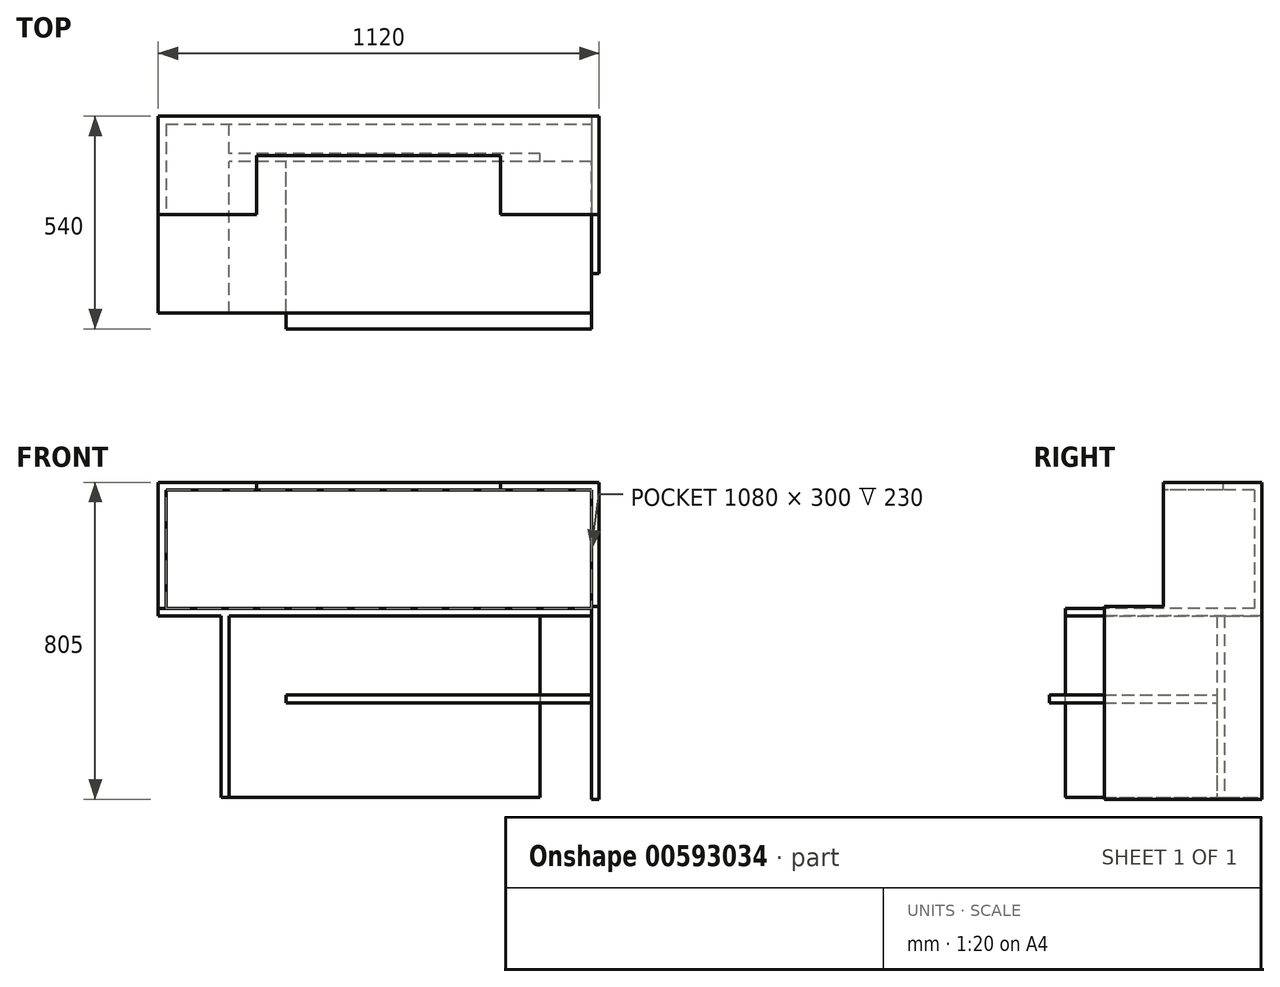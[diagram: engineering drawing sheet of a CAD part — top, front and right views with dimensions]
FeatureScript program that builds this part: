
annotation { "Feature Type Name" : "Feature", "Feature Type Description" : "" }
export const myFeature = defineFeature(function(context is Context, id is Id, definition is map)
    precondition{}
    {
        {
            var Q0;
            Q0=qCreatedBy(makeId("Top.planeOp"),FACE);
            var sketch = newSketch(context, id + "F0", { "sketchPlane" : qUnion([Q0])});
            skLineSegment(sketch, "E0.bottom", {"start": v(550, 250) * mm, "end": v(-550, 250) * mm});
            skLineSegment(sketch, "E0.top", {"start": v(550, -250) * mm, "end": v(-550, -250) * mm});
            skLineSegment(sketch, "E0.left", {"start": v(550, 250) * mm, "end": v(550, -250) * mm});
            skLineSegment(sketch, "E0.right", {"start": v(-550, 250) * mm, "end": v(-550, -250) * mm});
            skPoint(sketch, "E0.middle", {"position": v(0, 0) * mm});
            skSolve(sketch);
        }
        {
            var Q0;
            Q0=makeQuery(id+"F0.imprint","IMPRINT",FACE,{"disambiguationData":[TD([[makeQuery(id+"F0.imprint","IMPRINT",EDGE,{"derivedFrom":sQuery(id+"F0.wireOp",EDGE,"E0.bottom")}),1.0]])]});
            extrude(context, id + "F1", {"entities" : qUnion([Q0]), "depth" : 20 * mm, "offsetDistance" : 25 * mm});
        }
        {
            var Q0;
            Q0=qCreatedBy(makeId("Right.planeOp"),FACE);
            cPlane(context, id + "F2", {"entities" : qUnion([Q0]), "cplaneType" : CPlaneType.OFFSET, "offset" : 550 * mm, "width" : 150 * mm, "height" : 150 * mm});
        }
        {
            var Q0;
            Q0=qCreatedBy(id+"F2.planeOp",FACE);
            var sketch = newSketch(context, id + "F3", { "sketchPlane" : qUnion([Q0])});
            skLineSegment(sketch, "E1", {"start": v(250, 0) * mm, "end": v(250, 25) * mm});
            skLineSegment(sketch, "E2.bottom", {"start": v(250, 25) * mm, "end": v(-150, 25) * mm});
            skLineSegment(sketch, "E2.top", {"start": v(250, -465) * mm, "end": v(-150, -465) * mm});
            skLineSegment(sketch, "E2.left", {"start": v(250, 25) * mm, "end": v(250, -465) * mm});
            skLineSegment(sketch, "E2.right", {"start": v(-150, 25) * mm, "end": v(-150, -465) * mm});
            skSolve(sketch);
        }
        {
            var Q0;
            {var subQ0=sQuery(id+"F3.wireOp",EDGE,"E2.bottom");Q0=makeQuery(id+"F3.imprint","IMPRINT",FACE,{"disambiguationData":[TD([[makeQuery(id+"F3.imprint","IMPRINT",EDGE,{"derivedFrom":subQ0}),1.0]])]});}
            extrude(context, id + "F4", {"entities" : qUnion([Q0]), "operationType" : NewBodyOperationType.ADD, "depth" : 20 * mm, "offsetDistance" : 25 * mm});
        }
        {
            var Q0;
            Q0=makeQuery(id+"F0.imprint","IMPRINT",FACE,{"disambiguationData":[TD([[makeQuery(id+"F0.imprint","IMPRINT",EDGE,{"derivedFrom":sQuery(id+"F0.wireOp",EDGE,"E0.bottom")}),1.0]])]});
            var sketch = newSketch(context, id + "F5", { "sketchPlane" : qUnion([Q0])});
            skLineSegment(sketch, "E3.bottom", {"start": v(-370, -250) * mm, "end": v(-390, -250) * mm});
            skLineSegment(sketch, "E3.top", {"start": v(-370, 250) * mm, "end": v(-390, 250) * mm});
            skLineSegment(sketch, "E3.left", {"start": v(-370, -250) * mm, "end": v(-370, 250) * mm});
            skLineSegment(sketch, "E3.right", {"start": v(-390, -250) * mm, "end": v(-390, 250) * mm});
            skSolve(sketch);
        }
        {
            var Q0;
            Q0=makeQuery(id+"F5.imprint","IMPRINT",FACE,{"disambiguationData":[TD([[makeQuery(id+"F5.imprint","IMPRINT",EDGE,{"derivedFrom":sQuery(id+"F5.wireOp",EDGE,"E3.bottom")}),-1.0]])]});
            extrude(context, id + "F6", {"entities" : qUnion([Q0]), "operationType" : NewBodyOperationType.ADD, "oppositeDirection" : true, "depth" : 460 * mm, "offsetDistance" : 25 * mm});
        }
        {
            var Q0;
            Q0=makeQuery(id+"F6.boolean.opBoolean","MERGE",FACE,{"derivedFrom":[makeQuery(id+"F4.boolean.opBoolean","MERGE",FACE,{"derivedFrom":[makeQuery(id+"F1.opExtrude","SWEPT_FACE",FACE,{"disambiguationData":[OSD([sQuery(id+"F0.wireOp",EDGE,"E0.bottom")])]}),makeQuery(id+"F4.opExtrude","SWEPT_FACE",FACE,{"disambiguationData":[OSD([sQuery(id+"F3.wireOp",EDGE,"E2.left")])]})]}),makeQuery(id+"F6.opExtrude","SWEPT_FACE",FACE,{"disambiguationData":[OSD([sQuery(id+"F5.wireOp",EDGE,"E3.top")])]})]});
            cPlane(context, id + "F7", {"entities" : qUnion([Q0]), "cplaneType" : CPlaneType.OFFSET, "offset" : 95 * mm, "oppositeDirection" : true, "width" : 150 * mm, "height" : 150 * mm});
        }
        {
            var Q0;
            Q0=qCreatedBy(id+"F7.planeOp",FACE);
            var sketch = newSketch(context, id + "F8", { "sketchPlane" : qUnion([Q0])});
            skLineSegment(sketch, "E4", {"start": v(0, 0) * mm, "end": v(370, 0) * mm});
            skLineSegment(sketch, "E5.bottom", {"start": v(370, 0) * mm, "end": v(-420, 0) * mm});
            skLineSegment(sketch, "E5.top", {"start": v(370, -460) * mm, "end": v(-420, -460) * mm});
            skLineSegment(sketch, "E5.left", {"start": v(370, 0) * mm, "end": v(370, -460) * mm});
            skLineSegment(sketch, "E5.right", {"start": v(-420, 0) * mm, "end": v(-420, -460) * mm});
            skSolve(sketch);
        }
        {
            var Q0;
            Q0=makeQuery(id+"F8.imprint","IMPRINT",FACE,{"disambiguationData":[TD([[makeQuery(id+"F8.imprint","IMPRINT",EDGE,{"derivedFrom":sQuery(id+"F8.wireOp",EDGE,"E5.top")}),-1.0]])]});
            extrude(context, id + "F9", {"entities" : qUnion([Q0]), "operationType" : NewBodyOperationType.ADD, "oppositeDirection" : true, "depth" : 20 * mm, "offsetDistance" : 25 * mm});
        }
        {
            var Q0;
            Q0=makeQuery(id+"F9.opExtrude","CAP_FACE",FACE,{"disambiguationData":[OSD([sQuery(id+"F8.wireOp",EDGE,"E5.bottom"),sQuery(id+"F8.wireOp",EDGE,"E5.top"),sQuery(id+"F8.wireOp",EDGE,"E5.left"),sQuery(id+"F8.wireOp",EDGE,"E5.right")])],"isStart":false});
            var sketch = newSketch(context, id + "F10", { "sketchPlane" : qUnion([Q0])});
            skLineSegment(sketch, "E6.bottom", {"start": v(550, -200) * mm, "end": v(-225, -200) * mm});
            skLineSegment(sketch, "E6.top", {"start": v(550, -220) * mm, "end": v(-225, -220) * mm});
            skLineSegment(sketch, "E6.left", {"start": v(550, -200) * mm, "end": v(550, -220) * mm});
            skLineSegment(sketch, "E6.right", {"start": v(-225, -200) * mm, "end": v(-225, -220) * mm});
            skSolve(sketch);
        }
        {
            var Q0;
            Q0 = qSketchRegion(id + "F10", true);
            extrude(context, id + "F11", {"entities" : qUnion([Q0]), "operationType" : NewBodyOperationType.ADD, "depth" : 425 * mm, "offsetDistance" : 25 * mm});
        }
        {
            var Q0;
            Q0=makeQuery(id+"F1.opExtrude","CAP_FACE",FACE,{"disambiguationData":[OSD([sQuery(id+"F0.wireOp",EDGE,"E0.bottom"),sQuery(id+"F0.wireOp",EDGE,"E0.top"),sQuery(id+"F0.wireOp",EDGE,"E0.left"),sQuery(id+"F0.wireOp",EDGE,"E0.right")])],"isStart":false});
            var sketch = newSketch(context, id + "F12", { "sketchPlane" : qUnion([Q0])});
            skLineSegment(sketch, "E7.bottom", {"start": v(-550, 250) * mm, "end": v(550, 250) * mm});
            skLineSegment(sketch, "E7.top", {"start": v(-550, 230) * mm, "end": v(550, 230) * mm});
            skLineSegment(sketch, "E7.left", {"start": v(-550, 250) * mm, "end": v(-550, 230) * mm});
            skLineSegment(sketch, "E7.right", {"start": v(550, 250) * mm, "end": v(550, 230) * mm});
            skSolve(sketch);
        }
        {
            var Q0;
            Q0 = qSketchRegion(id + "F12", true);
            extrude(context, id + "F13", {"entities" : qUnion([Q0]), "operationType" : NewBodyOperationType.ADD, "depth" : 300 * mm, "offsetDistance" : 25 * mm});
        }
        {
            var Q0;
            Q0=makeQuery(id+"F1.opExtrude","CAP_FACE",FACE,{"disambiguationData":[OSD([sQuery(id+"F0.wireOp",EDGE,"E0.bottom"),sQuery(id+"F0.wireOp",EDGE,"E0.top"),sQuery(id+"F0.wireOp",EDGE,"E0.left"),sQuery(id+"F0.wireOp",EDGE,"E0.right")])],"isStart":false});
            var sketch = newSketch(context, id + "F14", { "sketchPlane" : qUnion([Q0])});
            skLineSegment(sketch, "E8.bottom", {"start": v(-550, 230) * mm, "end": v(-530, 230) * mm});
            skLineSegment(sketch, "E8.top", {"start": v(-550, 0) * mm, "end": v(-530, 0) * mm});
            skLineSegment(sketch, "E8.left", {"start": v(-550, 230) * mm, "end": v(-550, 0) * mm});
            skLineSegment(sketch, "E8.right", {"start": v(-530, 230) * mm, "end": v(-530, 0) * mm});
            skSolve(sketch);
        }
        {
            var Q0;
            Q0 = qSketchRegion(id + "F14", true);
            extrude(context, id + "F15", {"entities" : qUnion([Q0]), "operationType" : NewBodyOperationType.ADD, "depth" : 300 * mm, "offsetDistance" : 25 * mm});
        }
        {
            var Q0;
            Q0=makeQuery(id+"F4.opExtrude","SWEPT_FACE",FACE,{"disambiguationData":[OSD([sQuery(id+"F3.wireOp",EDGE,"E2.bottom")])]});
            var sketch = newSketch(context, id + "F16", { "sketchPlane" : qUnion([Q0])});
            skLineSegment(sketch, "E9.bottom", {"start": v(550, 250) * mm, "end": v(570, 250) * mm});
            skLineSegment(sketch, "E9.top", {"start": v(550, 0) * mm, "end": v(570, 0) * mm});
            skLineSegment(sketch, "E9.left", {"start": v(550, 250) * mm, "end": v(550, 0) * mm});
            skLineSegment(sketch, "E9.right", {"start": v(570, 250) * mm, "end": v(570, 0) * mm});
            skSolve(sketch);
        }
        {
            var Q0;
            Q0 = qSketchRegion(id + "F16", true);
            extrude(context, id + "F17", {"entities" : qUnion([Q0]), "operationType" : NewBodyOperationType.ADD, "depth" : 295 * mm, "offsetDistance" : 25 * mm});
        }
        {
            var Q0;
            Q0=makeQuery(id+"F17.boolean.opBoolean","MERGE",FACE,{"derivedFrom":[makeQuery(id+"F15.boolean.opBoolean","MERGE",FACE,{"derivedFrom":[makeQuery(id+"F13.opExtrude","CAP_FACE",FACE,{"disambiguationData":[OSD([sQuery(id+"F12.wireOp",EDGE,"E7.bottom"),sQuery(id+"F12.wireOp",EDGE,"E7.top"),sQuery(id+"F12.wireOp",EDGE,"E7.left"),sQuery(id+"F12.wireOp",EDGE,"E7.right")])],"isStart":false}),makeQuery(id+"F15.opExtrude","CAP_FACE",FACE,{"disambiguationData":[OSD([sQuery(id+"F14.wireOp",EDGE,"E8.bottom"),sQuery(id+"F14.wireOp",EDGE,"E8.top"),sQuery(id+"F14.wireOp",EDGE,"E8.left"),sQuery(id+"F14.wireOp",EDGE,"E8.right")])],"isStart":false})]}),makeQuery(id+"F17.opExtrude","CAP_FACE",FACE,{"disambiguationData":[OSD([sQuery(id+"F16.wireOp",EDGE,"E9.bottom"),sQuery(id+"F16.wireOp",EDGE,"E9.top"),sQuery(id+"F16.wireOp",EDGE,"E9.left"),sQuery(id+"F16.wireOp",EDGE,"E9.right")])],"isStart":false})]});
            var sketch = newSketch(context, id + "F18", { "sketchPlane" : qUnion([Q0])});
            skLineSegment(sketch, "E10", {"start": v(-550, 250) * mm, "end": v(-550, 0) * mm});
            skLineSegment(sketch, "E11", {"start": v(-550, 0) * mm, "end": v(-300, 0) * mm});
            skLineSegment(sketch, "E12", {"start": v(-550, 250) * mm, "end": v(-300, 250) * mm});
            skLineSegment(sketch, "E13", {"start": v(-300, 150) * mm, "end": v(-300, 0) * mm});
            skLineSegment(sketch, "E14.bottom", {"start": v(570, 250) * mm, "end": v(320, 250) * mm});
            skLineSegment(sketch, "E14.top", {"start": v(570, 0) * mm, "end": v(320, 0) * mm});
            skLineSegment(sketch, "E14.left", {"start": v(570, 250) * mm, "end": v(570, 0) * mm});
            skLineSegment(sketch, "E14.right", {"start": v(320, 150) * mm, "end": v(320, 0) * mm});
            skLineSegment(sketch, "E15", {"start": v(-300, 250) * mm, "end": v(320, 250) * mm});
            skLineSegment(sketch, "E16.0", {"start": v(-300, 150) * mm, "end": v(320, 150) * mm});
            skSolve(sketch);
        }
        {
            var Q0;
            Q0 = qSketchRegion(id + "F18", true);
            extrude(context, id + "F19", {"entities" : qUnion([Q0]), "operationType" : NewBodyOperationType.ADD, "depth" : 20 * mm, "offsetDistance" : 25 * mm});
        }
        {
            var Q0;
            Q0 = qSketchRegion(id + "F18", true);
            extrude(context, id + "F20", {"entities" : qUnion([Q0]), "operationType" : NewBodyOperationType.ADD, "depth" : 20 * mm, "offsetDistance" : 25 * mm});
        }
    });
